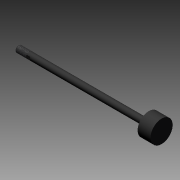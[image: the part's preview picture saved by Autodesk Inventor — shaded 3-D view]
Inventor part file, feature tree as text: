
AUTODESK INVENTOR PART (.ipt)
format: ipt  version: 2014 (Build 180170000, 170)  size: 162,816 bytes
history: native  units: in
note: dims shown in document units (in); Inventor stores cm internally (conversion verified against a paired STEP export)
features: other x98, sketch x3, revolve x2, thread x1, extrude x1
ambient origin geometry x8: Origin, YZ Plane, XZ Plane, XY Plane, X Axis, Y Axis, Z Axis, Center Point
bodies: Solid1 (feature_tree)
feature tree (105):
  revolve  "Revolution1"  Angle=360.0deg
  revolve  "Revolution2"  [1 undecoded]
  thread  "Thread1"  [1 undecoded]
  extrude  "Extrusion1"  [1 undecoded]
  other  "dia1_XY"
  other  "dia1_YZ"
  other  "dia1_ZX"
  other  "dia1_X"
  other  "dia1_Y"
  other  "dia1_Z"
  other  "dia1_Center"
  other  "dia12_XY"
  other  "dia12_YZ"
  other  "dia12_ZX"
  other  "dia12_X"
  other  "dia12_Y"
  other  "dia12_Z"
  other  "dia12_Center"
  other  "dia2_XY"
  other  "dia2_YZ"
  other  "dia2_ZX"
  other  "dia2_X"
  other  "dia2_Y"
  other  "dia2_Z"
  other  "dia2_Center"
  other  "dia22_XY"
  other  "dia22_YZ"
  other  "dia22_ZX"
  other  "dia22_X"
  other  "dia22_Y"
  other  "dia22_Z"
  other  "dia22_Center"
  other  "rl1_XY"
  other  "rl1_YZ"
  other  "rl1_ZX"
  other  "rl1_X"
  other  "rl1_Y"
  other  "rl1_Z"
  other  "rl1_Center"
  other  "rl2_XY"
  other  "rl2_YZ"
  other  "rl2_ZX"
  other  "rl2_X"
  other  "rl2_Y"
  other  "rl2_Z"
  other  "rl2_Center"
  other  "rod_cp_XY"
  other  "rod_cp_YZ"
  other  "rod_cp_ZX"
  other  "rod_cp_X"
  other  "rod_cp_Y"
  other  "rod_cp_Z"
  other  "rod_cp_Center"
  other  "thd1_XY"
  other  "thd1_YZ"
  other  "thd1_ZX"
  other  "thd1_X"
  other  "thd1_Y"
  other  "thd1_Z"
  other  "thd1_Center"
  other  "thd2_XY"
  other  "thd2_YZ"
  other  "thd2_ZX"
  other  "thd2_X"
  other  "thd2_Y"
  other  "thd2_Z"
  other  "thd2_Center"
  other  "to_rod_clevis_XY"
  other  "to_rod_clevis_YZ"
  other  "to_rod_clevis_ZX"
  other  "to_rod_clevis_X"
  other  "to_rod_clevis_Y"
  other  "to_rod_clevis_Z"
  other  "to_rod_clevis_Center"
  other  "wf1_XY"
  other  "wf1_YZ"
  other  "wf1_ZX"
  other  "wf1_X"
  other  "wf1_Y"
  other  "wf1_Z"
  other  "wf1_Center"
  other  "wf2_XY"
  other  "wf2_YZ"
  other  "wf2_ZX"
  other  "wf2_X"
  other  "wf2_Y"
  other  "wf2_Z"
  other  "wf2_Center"
  other  "wfw1_XY"
  other  "wfw1_YZ"
  other  "wfw1_ZX"
  other  "wfw1_X"
  other  "wfw1_Y"
  other  "wfw1_Z"
  other  "wfw1_Center"
  other  "wfw2_XY"
  other  "wfw2_YZ"
  other  "wfw2_ZX"
  other  "wfw2_X"
  other  "wfw2_Y"
  other  "wfw2_Z"
  other  "wfw2_Center"
  sketch  "Sketch_1"  dims[d0=360.0deg d1=360.0deg]
  sketch  "Sketch_3"  dims[d2=0.7203in d3=0.0in d4=0.25in d5=0.0in]
  sketch  "Sketch_10"
note: 3 required parameter values undecoded (feature->parameter linkage not recoverable at this tier; creation-order binding heuristic only, values carry confidence <= 0.55)